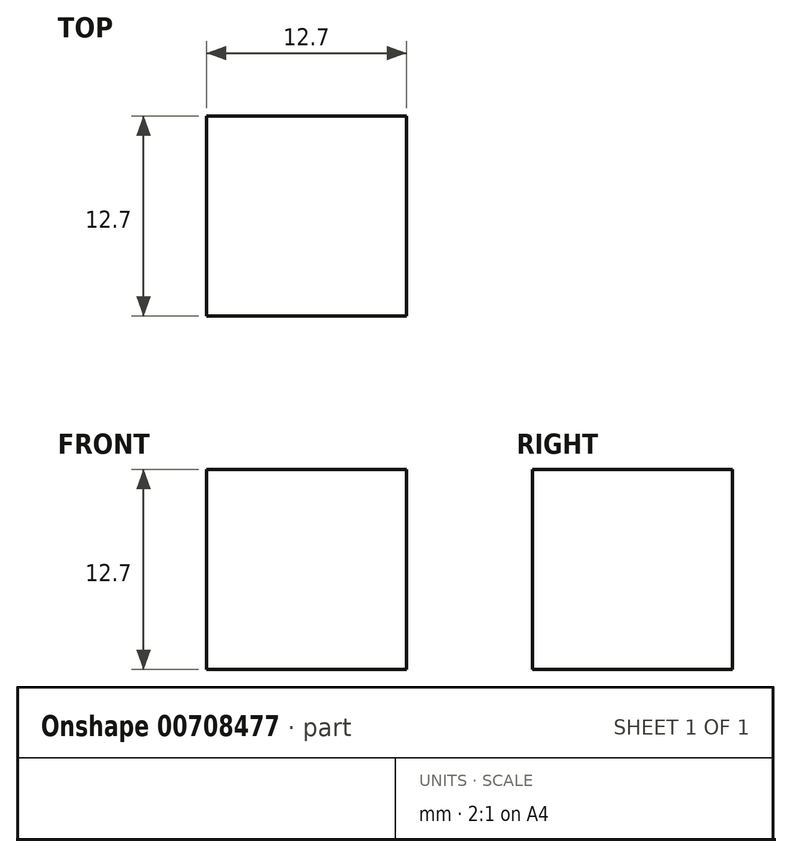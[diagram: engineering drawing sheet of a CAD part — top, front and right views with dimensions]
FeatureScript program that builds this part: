
annotation { "Feature Type Name" : "Feature", "Feature Type Description" : "" }
export const myFeature = defineFeature(function(context is Context, id is Id, definition is map)
    precondition{}
    {
        {
            var Q0;
            Q0=qCreatedBy(makeId("Front.planeOp"),FACE);
            var sketch = newSketch(context, id + "F0", { "sketchPlane" : qUnion([Q0])});
            skLineSegment(sketch, "E0.bottom", {"start": v(-6.35, -6.35) * mm, "end": v(6.35, -6.35) * mm});
            skLineSegment(sketch, "E0.top", {"start": v(-6.35, 6.35) * mm, "end": v(6.35, 6.35) * mm});
            skLineSegment(sketch, "E0.left", {"start": v(-6.35, -6.35) * mm, "end": v(-6.35, 6.35) * mm});
            skLineSegment(sketch, "E0.right", {"start": v(6.35, -6.35) * mm, "end": v(6.35, 6.35) * mm});
            skPoint(sketch, "E0.middle", {"position": v(0, 0) * mm});
            skSolve(sketch);
        }
        {
            var Q0;
            Q0 = qSketchRegion(id + "F0", true);
            extrude(context, id + "F1", {"entities" : qUnion([Q0]), "depth" : 12.7 * mm, "offsetDistance" : 25.4 * mm});
        }
    });
